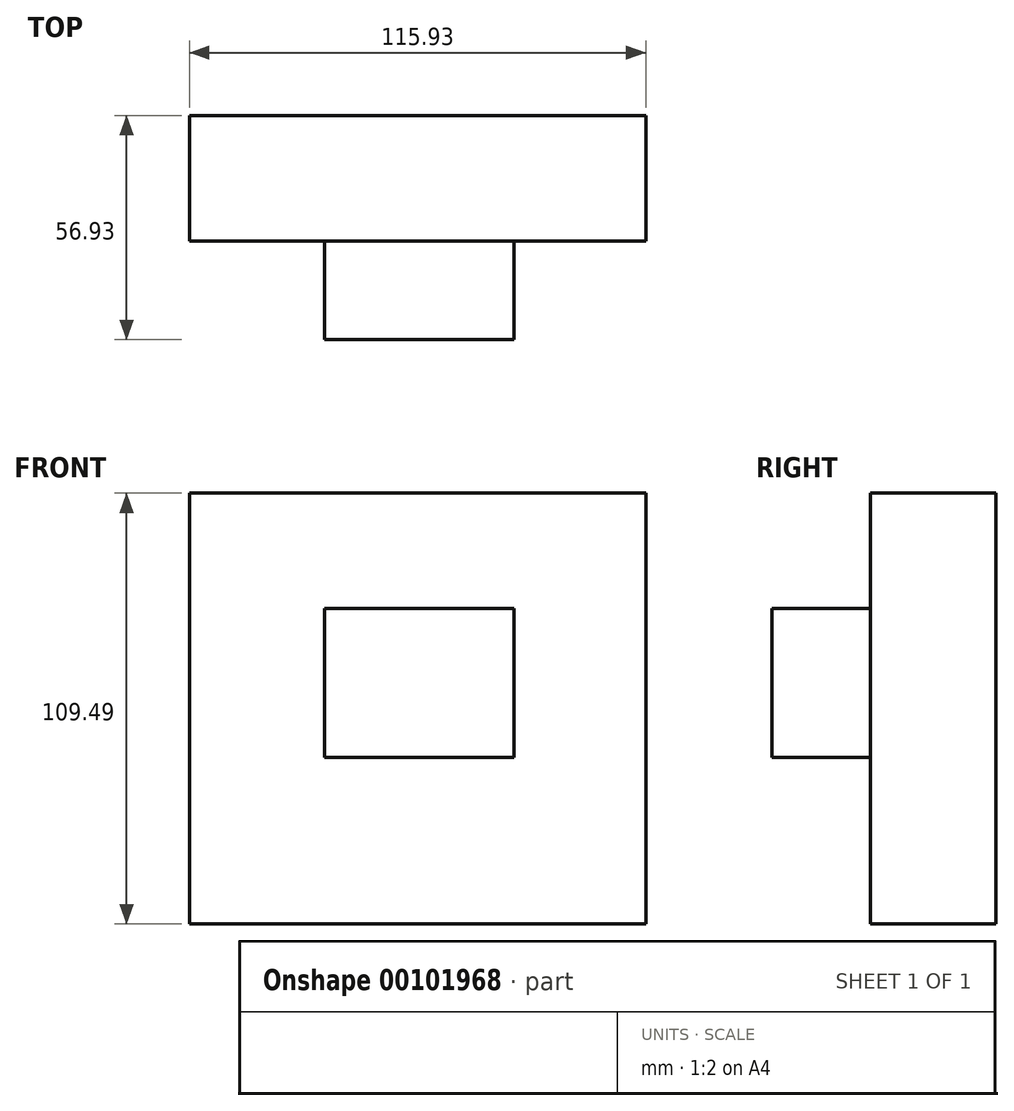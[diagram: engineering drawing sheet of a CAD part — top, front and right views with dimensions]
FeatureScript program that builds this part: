
annotation { "Feature Type Name" : "Feature", "Feature Type Description" : "" }
export const myFeature = defineFeature(function(context is Context, id is Id, definition is map)
    precondition{}
    {
        {
            var Q0;
            Q0=qCreatedBy(makeId("Front.planeOp"),FACE);
            var sketch = newSketch(context, id + "F0", { "sketchPlane" : qUnion([Q0])});
            skLineSegment(sketch, "E0.bottom", {"start": v(-56.8, 55.79) * mm, "end": v(59.12, 55.79) * mm});
            skLineSegment(sketch, "E0.top", {"start": v(-56.8, -53.7) * mm, "end": v(59.12, -53.7) * mm});
            skLineSegment(sketch, "E0.left", {"start": v(-56.8, 55.79) * mm, "end": v(-56.8, -53.7) * mm});
            skLineSegment(sketch, "E0.right", {"start": v(59.12, 55.79) * mm, "end": v(59.12, -53.7) * mm});
            skLineSegment(sketch, "E1.bottom", {"start": v(0, 17.24) * mm, "end": v(-28.84, 17.24) * mm});
            skLineSegment(sketch, "E1.top", {"start": v(0, -26.16) * mm, "end": v(-28.84, -26.16) * mm});
            skLineSegment(sketch, "E1.left", {"start": v(0, 17.24) * mm, "end": v(0, -26.16) * mm});
            skLineSegment(sketch, "E1.right", {"start": v(-28.84, 17.24) * mm, "end": v(-28.84, -26.16) * mm});
            skLineSegment(sketch, "E2", {"start": v(0, -26.16) * mm, "end": v(59.12, -53.7) * mm});
            skLineSegment(sketch, "E3", {"start": v(0, 17.24) * mm, "end": v(59.12, 55.79) * mm});
            skLineSegment(sketch, "E4", {"start": v(-28.84, 17.24) * mm, "end": v(-56.8, 55.79) * mm});
            skLineSegment(sketch, "E5", {"start": v(-28.84, -26.16) * mm, "end": v(-56.8, -53.7) * mm});
            skSolve(sketch);
        }
        {
            var Q0;
            Q0=makeQuery(id+"F0.imprint","IMPRINT",FACE,{"disambiguationData":[TD([[makeQuery(id+"F0.imprint","IMPRINT",EDGE,{"derivedFrom":sQuery(id+"F0.wireOp",EDGE,"E0.bottom")}),-1.0]])]});
            var Q1;
            Q1=makeQuery(id+"F0.imprint","IMPRINT",FACE,{"disambiguationData":[TD([[makeQuery(id+"F0.imprint","IMPRINT",EDGE,{"derivedFrom":sQuery(id+"F0.wireOp",EDGE,"E0.left")}),1.0]])]});
            var Q2;
            Q2=makeQuery(id+"F0.imprint","IMPRINT",FACE,{"disambiguationData":[TD([[makeQuery(id+"F0.imprint","IMPRINT",EDGE,{"derivedFrom":sQuery(id+"F0.wireOp",EDGE,"E0.top")}),1.0]])]});
            var Q3;
            Q3=makeQuery(id+"F0.imprint","IMPRINT",FACE,{"disambiguationData":[TD([[makeQuery(id+"F0.imprint","IMPRINT",EDGE,{"derivedFrom":sQuery(id+"F0.wireOp",EDGE,"E0.right")}),-1.0]])]});
            var Q4;
            Q4=makeQuery(id+"F0.imprint","IMPRINT",FACE,{"disambiguationData":[TD([[makeQuery(id+"F0.imprint","IMPRINT",EDGE,{"derivedFrom":sQuery(id+"F0.wireOp",EDGE,"E1.bottom")}),1.0]])]});
            extrude(context, id + "F1", {"entities" : qUnion([Q0, Q1, Q2, Q3, Q4]), "oppositeDirection" : true, "depth" : 31.93 * mm});
        }
        {
            var Q0;
            Q0=qCreatedBy(makeId("Front.planeOp"),FACE);
            var sketch = newSketch(context, id + "F2", { "sketchPlane" : qUnion([Q0])});
            skLineSegment(sketch, "E6.bottom", {"start": v(25.57, -11.37) * mm, "end": v(-22.56, -11.37) * mm});
            skLineSegment(sketch, "E6.top", {"start": v(25.57, 26.46) * mm, "end": v(-22.56, 26.46) * mm});
            skLineSegment(sketch, "E6.left", {"start": v(25.57, -11.37) * mm, "end": v(25.57, 26.46) * mm});
            skLineSegment(sketch, "E6.right", {"start": v(-22.56, -11.37) * mm, "end": v(-22.56, 26.46) * mm});
            skSolve(sketch);
        }
        {
            var Q0;
            Q0=makeQuery(id+"F2.imprint","IMPRINT",FACE,{"disambiguationData":[TD([[makeQuery(id+"F2.imprint","IMPRINT",EDGE,{"derivedFrom":sQuery(id+"F2.wireOp",EDGE,"E6.bottom")}),-1.0]])]});
            extrude(context, id + "F3", {"entities" : qUnion([Q0]), "operationType" : NewBodyOperationType.ADD, "depth" : 25 * mm});
        }
    });
